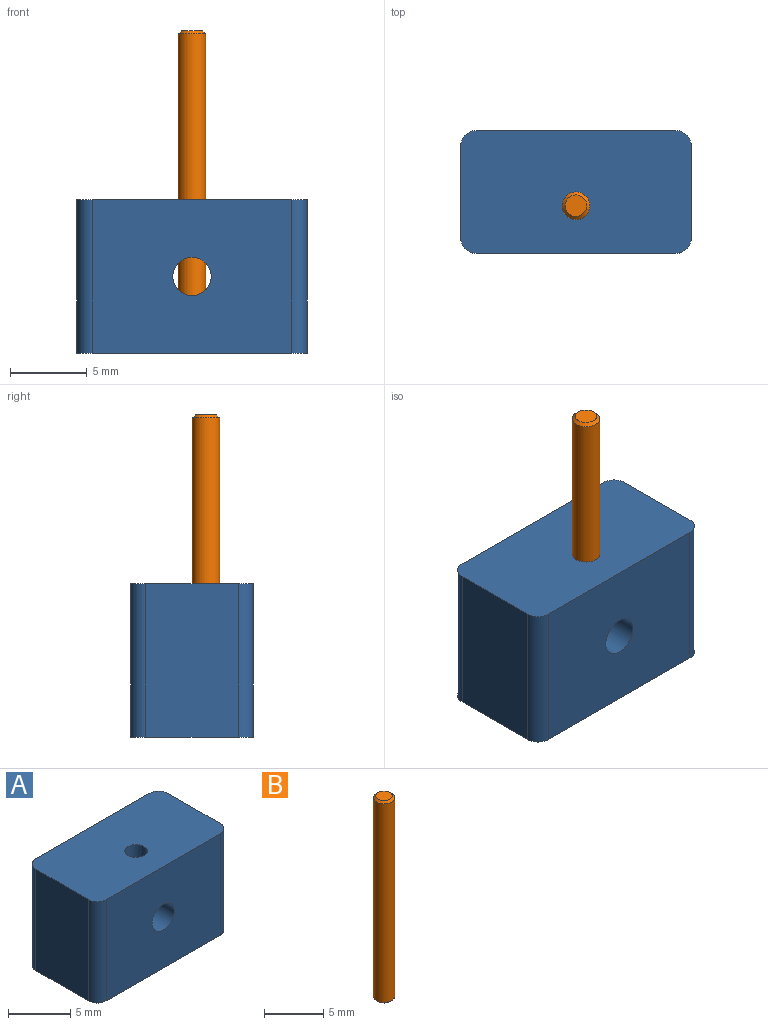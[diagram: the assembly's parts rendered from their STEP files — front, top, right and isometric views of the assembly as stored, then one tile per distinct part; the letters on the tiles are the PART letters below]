
ASSEMBLY  parts=2 mates=1
PART A: 13 faces, bbox 15x8x10 mm
  f0: cylinder r=0.9mm len=4.13mm, axis (0,0,1), area 22.2mm2, adj f2,f8
  f1: cylinder r=0.9mm len=4.13mm, axis (0,0,1), area 22.2mm2, adj f4,f8
  f2: plane 15x8mm, normal (0,0,-1), area 116.6mm2, adj f0,f3,f5,f6,f7,f9,f10,f11
  f3: plane 13x10mm, normal (0,1,0), area 125.1mm2, adj f2,f4,f8,f9,f11
  f4: plane 15x8mm, normal (0,0,1), area 116.6mm2, adj f1,f3,f5,f6,f7,f9,f10,f11
  f5: plane 13x10mm, normal (0,-1,0), area 125.1mm2, adj f2,f4,f8,f10,f12
  f6: plane 10x6mm, normal (1,0,0), area 60mm2, adj f2,f4,f11,f12
  f7: plane 10x6mm, normal (-1,0,0), area 60mm2, adj f2,f4,f9,f10
  f8: cylinder r=1.25mm len=8mm, axis (0,1,0), area 57.3mm2, adj f0,f1,f3,f5
  f9: cylinder r=1mm len=10mm, axis (0,0,1), area 15.7mm2, adj f2,f3,f4,f7
  f10: cylinder r=1mm len=10mm, axis (0,0,-1), area 15.7mm2, adj f2,f4,f5,f7
  f11: cylinder r=1mm len=10mm, axis (0,0,-1), area 15.7mm2, adj f2,f3,f4,f6
  f12: cylinder r=1mm len=10mm, axis (0,0,1), area 15.7mm2, adj f2,f4,f5,f6
PART B: 5 faces, bbox 1.8x1.8x21 mm
  f0: cylinder r=0.9mm len=20.6mm, axis (0,0,-1), area 116.5mm2, adj f3,f4
  f1: plane 1.4x1.4mm, normal (0,0,1), area 1.5mm2, adj f3
  f2: plane 1.4x1.4mm, normal (0,0,-1), area 1.5mm2, adj f4
  f3: cone r=0.7mm half-angle=45deg, axis (0,0,-1), area 1.4mm2, adj f0,f1
  f4: cone r=0.9mm half-angle=45deg, axis (0,0,1), area 1.4mm2, adj f0,f2
PLACE A t=(-98.54,-75.07,-10)mm
PLACE B t=(-98.54,-75.07,-10)mm
MATE fastened B.f0 <-> A.f0  axis (0,0,-1) through (0,-0.94,0)mm
